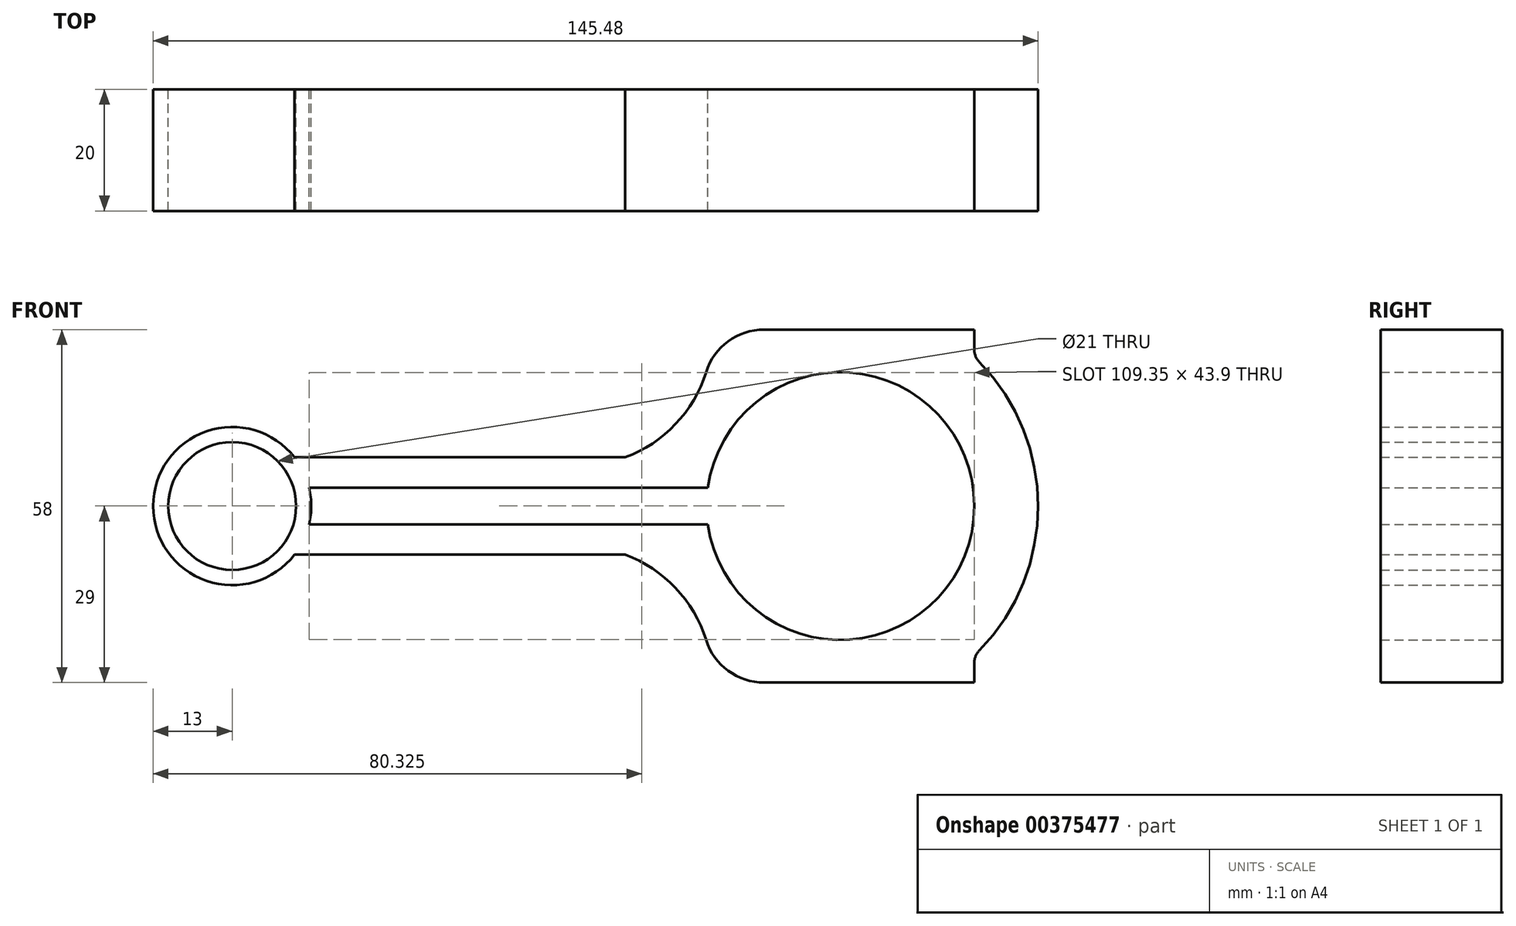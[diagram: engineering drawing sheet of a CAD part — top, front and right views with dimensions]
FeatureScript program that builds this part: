
annotation { "Feature Type Name" : "Feature", "Feature Type Description" : "" }
export const myFeature = defineFeature(function(context is Context, id is Id, definition is map)
    precondition{}
    {
        {
            var Q0;
            Q0=qCreatedBy(makeId("Front.planeOp"),FACE);
            var sketch = newSketch(context, id + "F0", { "sketchPlane" : qUnion([Q0])});
            skCircle(sketch, "E0", {"center": v(0, 0) * mm, "radius": 10.5 * mm});
            skCircle(sketch, "E1", {"center": v(0, 0) * mm, "radius": 13 * mm});
            skLineSegment(sketch, "E2", {"start": v(-13, 0) * mm, "end": v(134, 0) * mm, "construction": true});
            skPoint(sketch, "E3", {"position": v(16, 0) * mm});
            skPoint(sketch, "E4", {"position": v(-13, 0) * mm});
            skPoint(sketch, "E5.orphan", {"position": v(-47.4, 0) * mm});
            skPoint(sketch, "E6", {"position": v(122, 0) * mm});
            skCircle(sketch, "E7", {"center": v(100, 0) * mm, "radius": 22 * mm});
            skCircle(sketch, "E8", {"center": v(100, 0) * mm, "radius": 19 * mm});
            skLineSegment(sketch, "E9", {"start": v(100, 40.16) * mm, "end": v(100, -44.54) * mm, "construction": true});
            skPoint(sketch, "E10", {"position": v(76, 0) * mm});
            skLineSegment(sketch, "E11", {"start": v(10.25, 8) * mm, "end": v(79.5, 8) * mm});
            skLineSegment(sketch, "E12", {"start": v(12.65, 3) * mm, "end": v(78.2, 3) * mm});
            skLineSegment(sketch, "E13.MirrorCS", {"start": v(12.65, -3) * mm, "end": v(78.2, -3) * mm});
            skLineSegment(sketch, "E14.MirrorCS", {"start": v(10.25, -8) * mm, "end": v(79.5, -8) * mm});
            skLineSegment(sketch, "E15", {"start": v(87.46, 29) * mm, "end": v(122, 29) * mm});
            skArc(sketch, "E16", {"start": v(64.6, 8) * mm, "mid": v(72.88, 13.46) * mm, "end": v(77.92, 22) * mm});
            skPoint(sketch, "E17.visualSharp", {"position": v(78.93, 29) * mm});
            skArc(sketch, "E17.filletArc", {"start": v(87.46, 29) * mm, "mid": v(81.54, 27.06) * mm, "end": v(77.92, 22) * mm});
            skLineSegment(sketch, "E18", {"start": v(79.1, 24.5) * mm, "end": v(122, 24.5) * mm, "construction": true});
            skPoint(sketch, "E19", {"position": v(122, 29) * mm});
            skLineSegment(sketch, "E20", {"start": v(100, 19) * mm, "end": v(126.64, 19.01) * mm, "construction": true});
            skLineSegment(sketch, "E21.MirrorCS", {"start": v(87.46, -29) * mm, "end": v(122, -29) * mm});
            skArc(sketch, "E22.MirrorCS", {"start": v(87.46, -29) * mm, "mid": v(81.54, -27.06) * mm, "end": v(77.92, -22) * mm});
            skArc(sketch, "E23.MirrorCS", {"start": v(64.6, -8) * mm, "mid": v(72.88, -13.46) * mm, "end": v(77.92, -22) * mm});
            skPoint(sketch, "E24", {"position": v(118, 0) * mm});
            skLineSegment(sketch, "E25", {"start": v(122, 29) * mm, "end": v(122, 25.75) * mm});
            skPoint(sketch, "E26.newPointA", {"position": v(122, 22) * mm});
            skArc(sketch, "E26.filletArc", {"start": v(122, 24.56) * mm, "mid": v(122, 24.53) * mm, "end": v(122, 24.5) * mm});
            skLineSegment(sketch, "E27.MirrorCS", {"start": v(122, -29) * mm, "end": v(122, -25.8) * mm});
            skPoint(sketch, "E28", {"position": v(100, 27.5) * mm});
            skArc(sketch, "E29.trimOffspring", {"start": v(122.85, -23.71) * mm, "mid": v(132.48, -0.03) * mm, "end": v(122.85, 23.66) * mm});
            skLineSegment(sketch, "E30.trimOffspring", {"start": v(122, 24.5) * mm, "end": v(122.27, 24.5) * mm, "construction": true});
            skLineSegment(sketch, "E31.MirrorCS", {"start": v(79.1, -24.5) * mm, "end": v(122, -24.5) * mm, "construction": true});
            skPoint(sketch, "E32.visualSharp", {"position": v(122, -24.56) * mm});
            skArc(sketch, "E32.filletArc", {"start": v(122.85, -23.71) * mm, "mid": v(122.22, -24.68) * mm, "end": v(122, -25.8) * mm});
            skPoint(sketch, "E33.newPointB", {"position": v(122, 24.56) * mm});
            skArc(sketch, "E33.filletArc", {"start": v(122, 25.75) * mm, "mid": v(122.22, 24.62) * mm, "end": v(122.85, 23.66) * mm});
            skLineSegment(sketch, "E34.MirrorCS", {"start": v(100, 19) * mm, "end": v(76.73, 19) * mm, "construction": true});
            skPoint(sketch, "E35", {"position": v(76.73, 19) * mm});
            skSolve(sketch);
        }
        {
            var Q0;
            Q0 = qSketchRegion(id + "F0", true);
            extrude(context, id + "F1", {"entities" : qUnion([Q0]), "endBound" : BoundingType.SYMMETRIC, "depth" : 20 * mm});
        }
    });
